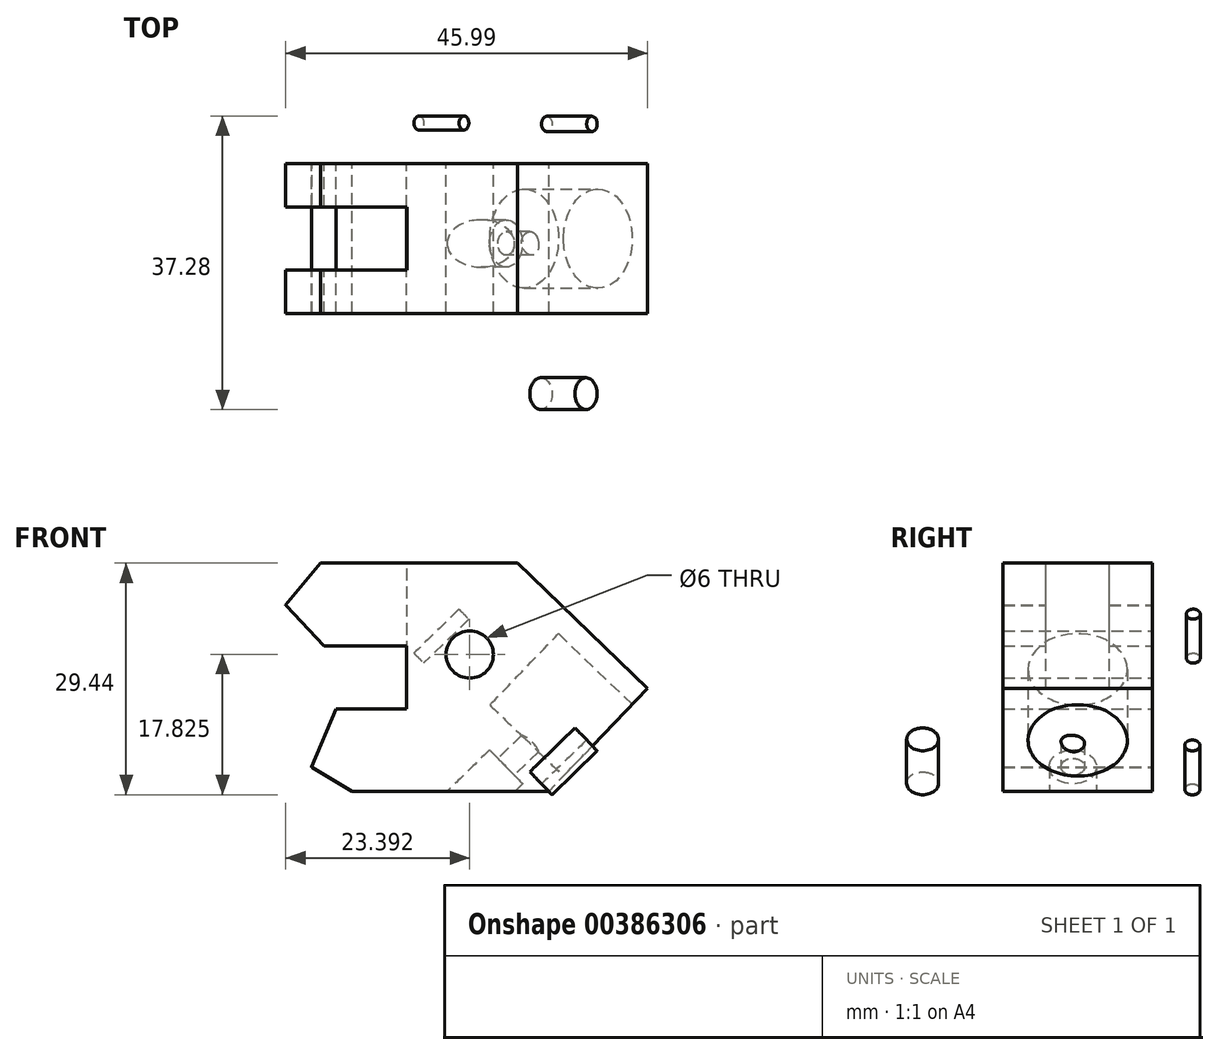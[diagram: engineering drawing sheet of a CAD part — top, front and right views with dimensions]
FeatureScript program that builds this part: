
annotation { "Feature Type Name" : "Feature", "Feature Type Description" : "" }
export const myFeature = defineFeature(function(context is Context, id is Id, definition is map)
    precondition{}
    {
        {
            var Q0;
            Q0=qCreatedBy(makeId("Front.planeOp"),FACE);
            var sketch = newSketch(context, id + "F0", { "sketchPlane" : qUnion([Q0])});
            skLineSegment(sketch, "E0", {"start": v(-71.85, 9.4) * mm, "end": v(-46.85, 9.4) * mm});
            skLineSegment(sketch, "E1", {"start": v(-67.85, -19.6) * mm, "end": v(-42.85, -19.6) * mm});
            skLineSegment(sketch, "E2", {"start": v(-46.85, 9.4) * mm, "end": v(-30.29, -6.55) * mm});
            skLineSegment(sketch, "E3", {"start": v(-30.29, -6.55) * mm, "end": v(-42.85, -19.6) * mm});
            skLineSegment(sketch, "E4", {"start": v(-60.89, -1.1) * mm, "end": v(-60.89, -9.1) * mm});
            skLineSegment(sketch, "E5", {"start": v(-71.39, -1.1) * mm, "end": v(-60.89, -1.1) * mm});
            skLineSegment(sketch, "E6", {"start": v(-69.89, -9.1) * mm, "end": v(-60.89, -9.1) * mm});
            skArc(sketch, "E7", {"start": v(-76.28, 4.05) * mm, "mid": v(-76.27, 4.04) * mm, "end": v(-76.25, 4.02) * mm});
            skArc(sketch, "E8", {"start": v(-76.25, 4.02) * mm, "mid": v(-76.25, 4.02) * mm, "end": v(-76.25, 4.02) * mm});
            skLineSegment(sketch, "E9", {"start": v(-71.85, 9.4) * mm, "end": v(-76.28, 4.05) * mm});
            skLineSegment(sketch, "E10", {"start": v(-76.28, 4.05) * mm, "end": v(-71.39, -1.1) * mm});
            skArc(sketch, "E11", {"start": v(-73, -16.52) * mm, "mid": v(-72.96, -16.53) * mm, "end": v(-72.93, -16.54) * mm});
            skArc(sketch, "E12", {"start": v(-72.93, -16.54) * mm, "mid": v(-72.93, -16.55) * mm, "end": v(-72.94, -16.55) * mm});
            skLineSegment(sketch, "E13", {"start": v(-69.89, -9.1) * mm, "end": v(-73, -16.52) * mm});
            skLineSegment(sketch, "E14", {"start": v(-73, -16.52) * mm, "end": v(-67.85, -19.6) * mm});
            skCircle(sketch, "E15", {"center": v(-52.89, -2.22) * mm, "radius": 3 * mm});
            skSolve(sketch);
        }
        {
            var Q0;
            Q0=makeQuery(id+"F0.imprint","IMPRINT",FACE,{"disambiguationData":[TD([[makeQuery(id+"F0.imprint","IMPRINT",EDGE,{"derivedFrom":sQuery(id+"F0.wireOp",EDGE,"E0")}),-1.0]])]});
            extrude(context, id + "F1", {"entities" : qUnion([Q0]), "depth" : 19 * mm});
        }
        {
            var Q0;
            Q0=makeQuery(id+"F1.opExtrude","SWEPT_FACE",FACE,{"disambiguationData":[OSD([sQuery(id+"F0.wireOp",EDGE,"E0")])]});
            var sketch = newSketch(context, id + "F2", { "sketchPlane" : qUnion([Q0])});
            skLineSegment(sketch, "E16", {"start": v(-29.52, -5.5) * mm, "end": v(-97.4, -5.5) * mm});
            skLineSegment(sketch, "E17", {"start": v(-28.86, -13.5) * mm, "end": v(-100.5, -13.5) * mm});
            skLineSegment(sketch, "E18", {"start": v(-97.4, -5.5) * mm, "end": v(-97.4, -13.5) * mm});
            skLineSegment(sketch, "E19", {"start": v(-60.85, -5.5) * mm, "end": v(-60.85, -13.5) * mm});
            skSolve(sketch);
        }
        {
            var Q0;
            {var subQ0=sQuery(id+"F2.wireOp",EDGE,"E19");Q0=makeQuery(id+"F2.imprint","IMPRINT",FACE,{"disambiguationData":[TD([[makeQuery(id+"F2.imprint","IMPRINT",EDGE,{"derivedFrom":subQ0}),-1.0]])]});}
            var Q1;
            {var subQ0=sQuery(id+"F2.wireOp",EDGE,"E18");Q1=makeQuery(id+"F2.imprint","IMPRINT",FACE,{"disambiguationData":[TD([[makeQuery(id+"F2.imprint","IMPRINT",EDGE,{"derivedFrom":subQ0}),1.0]])]});}
            extrude(context, id + "F3", {"entities" : qUnion([Q0, Q1]), "operationType" : NewBodyOperationType.REMOVE, "oppositeDirection" : true, "depth" : 16 * mm});
        }
        {
            var Q0;
            Q0=makeQuery(id+"F1.opExtrude","SWEPT_FACE",FACE,{"disambiguationData":[OSD([sQuery(id+"F0.wireOp",EDGE,"E3")])]});
            var sketch = newSketch(context, id + "F4", { "sketchPlane" : qUnion([Q0])});
            skCircle(sketch, "E20", {"center": v(-9.5, -34.85) * mm, "radius": 6.3 * mm});
            skSolve(sketch);
        }
        {
            var Q0;
            Q0=qSketchRegion(id+"F4",true);
            var Q1;
            {var subQ0=sQuery(id+"F0.wireOp",EDGE,"obgSHjAs-CF7U-fFNJ-GP6A-8ZxQo6zeKuEo");Q1=makeQuery(id+"F1.opExtrude","SWEPT_FACE",FACE,{"disambiguationData":[OSD([subQ0]),TDD([makeQuery(id+"F0.imprint","IMPRINT",EDGE,{"disambiguationData":[TD([[makeQuery(id+"F0.imprint","INTERSECT",VERTEX,{"derivedFrom":[sQuery(id+"F0.wireOp",EDGE,"E4"),subQ0]}),1.0]])],"derivedFrom":subQ0})])]});}
            extrude(context, id + "F5", {"entities" : qUnion([Q0, Q1]), "operationType" : NewBodyOperationType.REMOVE, "oppositeDirection" : true, "depth" : 13 * mm});
        }
        {
            var Q0;
            Q0=makeQuery(id+"F1.opExtrude","CAP_VERTEX",VERTEX,{"disambiguationData":[OSD([sQuery(id+"F0.wireOp",EDGE,"E1"),sQuery(id+"F0.wireOp",EDGE,"E3")])],"isStart":false});
            var Q1;
            Q1=makeQuery(id+"F1.opExtrude","CAP_VERTEX",VERTEX,{"disambiguationData":[OSD([sQuery(id+"F0.wireOp",EDGE,"E1"),sQuery(id+"F0.wireOp",EDGE,"E3")])],"isStart":true});
            var Q2;
            Q2=makeQuery(id+"F1.opExtrude","CAP_VERTEX",VERTEX,{"disambiguationData":[OSD([sQuery(id+"F0.wireOp",EDGE,"E4"),sQuery(id+"F0.wireOp",EDGE,"E5")])],"isStart":false});
            cPlane(context, id + "F6", {"entities" : qUnion([Q0, Q1, Q2]), "cplaneType" : CPlaneType.THREE_POINT, "offset" : 25 * mm, "width" : 150 * mm, "height" : 150 * mm});
        }
        {
            var Q0;
            Q0=qCreatedBy(id+"F6.planeOp",FACE);
            var sketch = newSketch(context, id + "F7", { "sketchPlane" : qUnion([Q0])});
            skCircle(sketch, "E21", {"center": v(-5.07, 16.23) * mm, "radius": 0.96 * mm});
            skCircle(sketch, "E22", {"center": v(-5.18, 39.52) * mm, "radius": 0.89 * mm});
            skCircle(sketch, "E23", {"center": v(29.2, 17.3) * mm, "radius": 2.02 * mm});
            skSolve(sketch);
        }
        {
            var Q0;
            Q0=makeQuery(id+"F7.imprint","IMPRINT",FACE,{"disambiguationData":[TD([[makeQuery(id+"F7.imprint","IMPRINT",EDGE,{"derivedFrom":sQuery(id+"F7.wireOp",EDGE,"E23")}),1.0]])]});
            var Q1;
            Q1=makeQuery(id+"F7.imprint","IMPRINT",FACE,{"disambiguationData":[TD([[makeQuery(id+"F7.imprint","IMPRINT",EDGE,{"derivedFrom":sQuery(id+"F7.wireOp",EDGE,"E21")}),1.0]])]});
            var Q2;
            Q2=makeQuery(id+"F7.imprint","IMPRINT",FACE,{"disambiguationData":[TD([[makeQuery(id+"F7.imprint","IMPRINT",EDGE,{"derivedFrom":sQuery(id+"F7.wireOp",EDGE,"E22")}),1.0]])]});
            extrude(context, id + "F8", {"entities" : qUnion([Q0, Q1, Q2]), "oppositeDirection" : true, "depth" : 8 * mm});
        }
        {
            var Q0;
            Q0=makeQuery(id+"F8.opExtrude","CAP_FACE",FACE,{"disambiguationData":[OSD([sQuery(id+"F7.wireOp",EDGE,"E23")])],"isStart":false});
            var sketch = newSketch(context, id + "F9", { "sketchPlane" : qUnion([Q0])});
            skCircle(sketch, "E24", {"center": v(-10.12, 21.9) * mm, "radius": 1.5 * mm});
            skLineSegment(sketch, "E25", {"start": v(-10.12, 15.9) * mm, "end": v(-10.12, 30.7) * mm});
            skCircle(sketch, "E26", {"center": v(-10.12, 21.9) * mm, "radius": 3 * mm});
            skPoint(sketch, "E27", {"position": v(-10.12, 23.4) * mm});
            skSolve(sketch);
        }
        {
            var Q0;
            {var subQ0=sQuery(id+"F9.wireOp",EDGE,"E25");var subQ1=sQuery(id+"F9.wireOp",EDGE,"E24");var subQ2=makeQuery(id+"F9.imprint","INTERSECT",VERTEX,{"disambiguationData":[OD(0.0)],"derivedFrom":[subQ1,subQ0]});Q0=makeQuery(id+"F9.imprint","IMPRINT",FACE,{"disambiguationData":[TD([[makeQuery(id+"F9.imprint","IMPRINT",EDGE,{"disambiguationData":[TD([[subQ2,-1.0]])],"derivedFrom":subQ1}),1.0]])]});}
            var Q1;
            {var subQ0=sQuery(id+"F9.wireOp",EDGE,"E25");var subQ1=sQuery(id+"F9.wireOp",EDGE,"E24");var subQ2=makeQuery(id+"F9.imprint","INTERSECT",VERTEX,{"disambiguationData":[OD(0.0)],"derivedFrom":[subQ1,subQ0]});Q1=makeQuery(id+"F9.imprint","IMPRINT",FACE,{"disambiguationData":[TD([[makeQuery(id+"F9.imprint","IMPRINT",EDGE,{"disambiguationData":[TD([[subQ2,1.0]])],"derivedFrom":subQ1}),1.0]])]});}
            extrude(context, id + "F10", {"entities" : qUnion([Q0, Q1]), "operationType" : NewBodyOperationType.ADD, "oppositeDirection" : true, "depth" : 25 * mm});
        }
        {
            var Q0;
            Q0=makeQuery(id+"F10.opExtrude","CAP_FACE",FACE,{"disambiguationData":[OSD([sQuery(id+"F9.wireOp",EDGE,"E24")])],"isStart":false});
            var sketch = newSketch(context, id + "F11", { "sketchPlane" : qUnion([Q0])});
            skCircle(sketch, "E28", {"center": v(10.12, 21.9) * mm, "radius": 3 * mm});
            skLineSegment(sketch, "E29", {"start": v(10.12, 21.9) * mm, "end": v(10.12, -18.39) * mm});
            skSolve(sketch);
        }
        {
            var Q0;
            Q0=makeQuery(id+"F11.imprint","IMPRINT",FACE,{"disambiguationData":[TD([[makeQuery(id+"F11.imprint","IMPRINT",EDGE,{"derivedFrom":makeQuery(id+"F10.opExtrude","CAP_EDGE",EDGE,{"disambiguationData":[OSD([sQuery(id+"F9.wireOp",EDGE,"E24")])],"isStart":false})}),-1.0]])]});
            extrude(context, id + "F12", {"entities" : qUnion([Q0]), "operationType" : NewBodyOperationType.REMOVE, "oppositeDirection" : true, "depth" : 25 * mm});
        }
        {
            var Q0;
            Q0=makeQuery(id+"F1.opExtrude","SWEPT_FACE",FACE,{"disambiguationData":[OSD([sQuery(id+"F0.wireOp",EDGE,"E1")])]});
            var sketch = newSketch(context, id + "F13", { "sketchPlane" : qUnion([Q0])});
            skLineSegment(sketch, "E30", {"start": v(-53.62, 0) * mm, "end": v(-53.62, 19) * mm});
            skPoint(sketch, "E30.startSnap0", {"position": v(-53.62, 10.12) * mm});
            skSolve(sketch);
        }
        {
            var Q0;
            Q0=sQuery(id+"F13.wireOp",VERTEX,"E30.startSnap0");
            var Q1;
            Q1=qCreatedBy(id+"F6.planeOp",FACE);
            cPlane(context, id + "F14", {"entities" : qUnion([Q0, Q1]), "cplaneType" : CPlaneType.PLANE_POINT, "offset" : 25 * mm, "width" : 150 * mm, "height" : 150 * mm});
        }
        {
            var Q0;
            Q0=qCreatedBy(id+"F14.planeOp",FACE);
            var sketch = newSketch(context, id + "F15", { "sketchPlane" : qUnion([Q0])});
            skCircle(sketch, "E31.0", {"center": v(10.12, 21.9) * mm, "radius": 1.5 * mm});
            skCircle(sketch, "E32", {"center": v(10.12, 21.9) * mm, "radius": 3 * mm});
            skSolve(sketch);
        }
        {
            var Q0;
            Q0=makeQuery(id+"F15.imprint","IMPRINT",FACE,{"disambiguationData":[TD([[makeQuery(id+"F15.imprint","IMPRINT",EDGE,{"derivedFrom":sQuery(id+"F15.wireOp",EDGE,"E31.0")}),-1.0]])]});
            extrude(context, id + "F16", {"entities" : qUnion([Q0]), "operationType" : NewBodyOperationType.REMOVE, "oppositeDirection" : true, "depth" : 6 * mm, "hasSecondDirection" : true, "secondDirectionBound" : BoundingType.THROUGH_ALL, "secondDirectionOppositeDirection" : false, "secondDirectionDepth" : 0 * mm});
        }
    });
